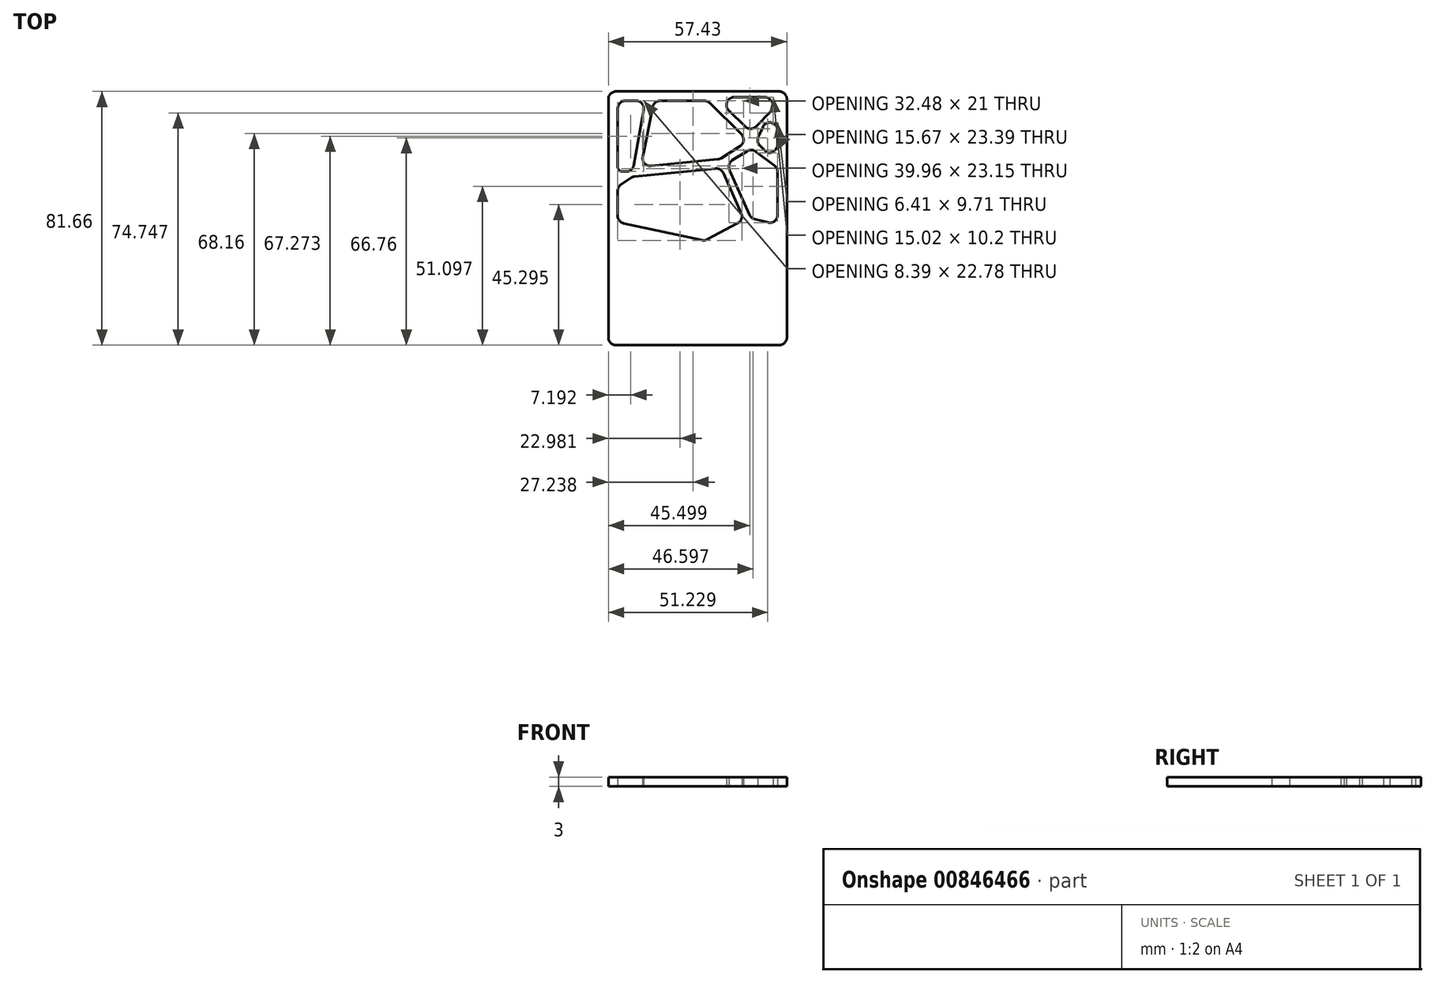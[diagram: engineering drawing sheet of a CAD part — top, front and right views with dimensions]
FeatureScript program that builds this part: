
annotation { "Feature Type Name" : "Feature", "Feature Type Description" : "" }
export const myFeature = defineFeature(function(context is Context, id is Id, definition is map)
    precondition{}
    {
        {
            assignVariable(context, id + "F0", {"name" : "depth", "anyValue" : 3 * mm});
        }
        {
            var Q0;
            Q0=qCreatedBy(makeId("Top.planeOp"),FACE);
            var sketch = newSketch(context, id + "F1", { "sketchPlane" : qUnion([Q0])});
            skLineSegment(sketch, "E0", {"start": v(11.17, 31.6) * mm, "end": v(14.38, 33.7) * mm});
            skLineSegment(sketch, "E1", {"start": v(15.5, 34.1) * mm, "end": v(41.49, 36.69) * mm});
            skLineSegment(sketch, "E2", {"start": v(44.02, 35.22) * mm, "end": v(49.79, 22.3) * mm});
            skLineSegment(sketch, "E3", {"start": v(48.68, 19.07) * mm, "end": v(38.89, 13.85) * mm});
            skLineSegment(sketch, "E4", {"start": v(37.19, 13.6) * mm, "end": v(12.02, 19) * mm});
            skPoint(sketch, "E5.visualSharp", {"position": v(21.18, 34.67) * mm});
            skArc(sketch, "E5.filletArc", {"start": v(15.5, 34.1) * mm, "mid": v(14.91, 33.97) * mm, "end": v(14.38, 33.7) * mm});
            skPoint(sketch, "E6.visualSharp", {"position": v(43.28, 36.87) * mm});
            skArc(sketch, "E6.filletArc", {"start": v(44.02, 35.22) * mm, "mid": v(43, 36.36) * mm, "end": v(41.49, 36.69) * mm});
            skPoint(sketch, "E7.visualSharp", {"position": v(50.74, 20.17) * mm});
            skArc(sketch, "E7.filletArc", {"start": v(48.68, 19.07) * mm, "mid": v(49.87, 20.46) * mm, "end": v(49.79, 22.3) * mm});
            skPoint(sketch, "E8.visualSharp", {"position": v(38.08, 13.41) * mm});
            skArc(sketch, "E8.filletArc", {"start": v(37.19, 13.6) * mm, "mid": v(38.06, 13.58) * mm, "end": v(38.89, 13.85) * mm});
            skLineSegment(sketch, "E9", {"start": v(20.79, 37.49) * mm, "end": v(42.17, 39.62) * mm});
            skLineSegment(sketch, "E10", {"start": v(43.27, 40) * mm, "end": v(49.37, 43.86) * mm});
            skLineSegment(sketch, "E11", {"start": v(49.78, 47.76) * mm, "end": v(39.55, 57.78) * mm});
            skLineSegment(sketch, "E12", {"start": v(37.8, 58.5) * mm, "end": v(23.76, 58.5) * mm});
            skLineSegment(sketch, "E13", {"start": v(21.3, 56.48) * mm, "end": v(18.09, 40.47) * mm});
            skPoint(sketch, "E14.visualSharp", {"position": v(21.7, 58.5) * mm});
            skArc(sketch, "E14.filletArc", {"start": v(23.76, 58.5) * mm, "mid": v(22.17, 57.93) * mm, "end": v(21.3, 56.48) * mm});
            skPoint(sketch, "E15.visualSharp", {"position": v(17.42, 37.15) * mm});
            skArc(sketch, "E15.filletArc", {"start": v(18.09, 40.47) * mm, "mid": v(18.69, 38.3) * mm, "end": v(20.79, 37.49) * mm});
            skPoint(sketch, "E16.visualSharp", {"position": v(42.76, 39.68) * mm});
            skArc(sketch, "E16.filletArc", {"start": v(42.17, 39.62) * mm, "mid": v(42.74, 39.74) * mm, "end": v(43.27, 40) * mm});
            skPoint(sketch, "E17.visualSharp", {"position": v(38.82, 58.5) * mm});
            skArc(sketch, "E17.filletArc", {"start": v(39.55, 57.78) * mm, "mid": v(38.75, 58.3) * mm, "end": v(37.8, 58.5) * mm});
            skPoint(sketch, "E18.visualSharp", {"position": v(52.03, 45.55) * mm});
            skArc(sketch, "E18.filletArc", {"start": v(49.37, 43.86) * mm, "mid": v(50.52, 45.71) * mm, "end": v(49.78, 47.76) * mm});
            skPoint(sketch, "E19", {"position": v(30.78, 58.5) * mm});
            skLineSegment(sketch, "E20", {"start": v(47, 39.4) * mm, "end": v(51.65, 42.26) * mm});
            skLineSegment(sketch, "E21", {"start": v(46.01, 36.26) * mm, "end": v(52.48, 21.76) * mm});
            skLineSegment(sketch, "E22", {"start": v(54.16, 20.35) * mm, "end": v(58.37, 19.3) * mm});
            skLineSegment(sketch, "E23", {"start": v(61.47, 21.73) * mm, "end": v(61.47, 33.28) * mm});
            skLineSegment(sketch, "E24", {"start": v(61.47, 33.32) * mm, "end": v(61.44, 35.64) * mm});
            skLineSegment(sketch, "E25", {"start": v(60.45, 37.6) * mm, "end": v(54.46, 42.12) * mm});
            skPoint(sketch, "E26.visualSharp", {"position": v(53.1, 43.15) * mm});
            skArc(sketch, "E26.filletArc", {"start": v(54.46, 42.12) * mm, "mid": v(53.08, 42.62) * mm, "end": v(51.65, 42.26) * mm});
            skPoint(sketch, "E27.visualSharp", {"position": v(45.12, 38.26) * mm});
            skArc(sketch, "E27.filletArc", {"start": v(47, 39.4) * mm, "mid": v(45.9, 38.02) * mm, "end": v(46.01, 36.26) * mm});
            skPoint(sketch, "E28.visualSharp", {"position": v(52.98, 20.65) * mm});
            skArc(sketch, "E28.filletArc", {"start": v(52.48, 21.76) * mm, "mid": v(53.16, 20.86) * mm, "end": v(54.16, 20.35) * mm});
            skPoint(sketch, "E29.visualSharp", {"position": v(61.47, 18.53) * mm});
            skArc(sketch, "E29.filletArc", {"start": v(58.37, 19.3) * mm, "mid": v(60.51, 19.76) * mm, "end": v(61.47, 21.73) * mm});
            skPoint(sketch, "E30.visualSharp", {"position": v(61.47, 33.3) * mm});
            skArc(sketch, "E30.filletArc", {"start": v(61.47, 33.28) * mm, "mid": v(61.47, 33.3) * mm, "end": v(61.47, 33.32) * mm});
            skPoint(sketch, "E31.visualSharp", {"position": v(61.42, 36.87) * mm});
            skArc(sketch, "E31.filletArc", {"start": v(61.44, 35.64) * mm, "mid": v(61.17, 36.74) * mm, "end": v(60.45, 37.6) * mm});
            skLineSegment(sketch, "E32", {"start": v(10.04, 21.45) * mm, "end": v(10.04, 29.51) * mm});
            skPoint(sketch, "E33.visualSharp", {"position": v(10.04, 30.86) * mm});
            skArc(sketch, "E33.filletArc", {"start": v(11.17, 31.6) * mm, "mid": v(10.34, 30.7) * mm, "end": v(10.04, 29.51) * mm});
            skLineSegment(sketch, "E34", {"start": v(7.04, 59) * mm, "end": v(7.04, -17.67) * mm});
            skLineSegment(sketch, "E35", {"start": v(64.47, -17.67) * mm, "end": v(64.47, 59) * mm});
            skPoint(sketch, "E36.visualSharp", {"position": v(10.04, 19.43) * mm});
            skArc(sketch, "E36.filletArc", {"start": v(10.04, 21.45) * mm, "mid": v(10.6, 19.88) * mm, "end": v(12.02, 19) * mm});
            skLineSegment(sketch, "E37", {"start": v(9.54, -20.17) * mm, "end": v(61.97, -20.17) * mm});
            skPoint(sketch, "E38.visualSharp", {"position": v(7.04, -20.17) * mm});
            skArc(sketch, "E38.filletArc", {"start": v(7.04, -17.67) * mm, "mid": v(7.77, -19.44) * mm, "end": v(9.54, -20.17) * mm});
            skPoint(sketch, "E39.visualSharp", {"position": v(64.47, -20.17) * mm});
            skArc(sketch, "E39.filletArc", {"start": v(61.97, -20.17) * mm, "mid": v(63.74, -19.44) * mm, "end": v(64.47, -17.67) * mm});
            skLineSegment(sketch, "E40", {"start": v(9.54, 61.5) * mm, "end": v(61.97, 61.5) * mm});
            skPoint(sketch, "E41.visualSharp", {"position": v(7.04, 61.5) * mm});
            skArc(sketch, "E41.filletArc", {"start": v(9.54, 61.5) * mm, "mid": v(7.77, 60.76) * mm, "end": v(7.04, 59) * mm});
            skPoint(sketch, "E42.visualSharp", {"position": v(64.47, 61.5) * mm});
            skArc(sketch, "E42.filletArc", {"start": v(64.47, 59) * mm, "mid": v(63.74, 60.76) * mm, "end": v(61.97, 61.5) * mm});
            skLineSegment(sketch, "E43", {"start": v(45.77, 55.34) * mm, "end": v(51.03, 50.2) * mm});
            skLineSegment(sketch, "E44", {"start": v(54.56, 50.23) * mm, "end": v(59.34, 55.1) * mm});
            skLineSegment(sketch, "E45", {"start": v(59.3, 58.64) * mm, "end": v(58.97, 58.96) * mm});
            skLineSegment(sketch, "E46", {"start": v(57.2, 59.68) * mm, "end": v(47.5, 59.63) * mm});
            skLineSegment(sketch, "E47", {"start": v(55.81, 43.98) * mm, "end": v(57.52, 42.3) * mm});
            skLineSegment(sketch, "E48", {"start": v(60.35, 42.34) * mm, "end": v(60.76, 42.75) * mm});
            skLineSegment(sketch, "E49", {"start": v(61.47, 44.5) * mm, "end": v(61.47, 48.97) * mm});
            skLineSegment(sketch, "E50", {"start": v(56.69, 49.98) * mm, "end": v(55.27, 46.78) * mm});
            skLineSegment(sketch, "E51", {"start": v(18.39, 55.56) * mm, "end": v(15.25, 37.78) * mm});
            skLineSegment(sketch, "E52", {"start": v(12.79, 35.71) * mm, "end": v(11.54, 35.71) * mm});
            skLineSegment(sketch, "E53", {"start": v(10.04, 37.21) * mm, "end": v(10.04, 56) * mm});
            skLineSegment(sketch, "E54", {"start": v(12.54, 58.5) * mm, "end": v(15.93, 58.5) * mm});
            skPoint(sketch, "E55.visualSharp", {"position": v(10.04, 58.5) * mm});
            skArc(sketch, "E55.filletArc", {"start": v(12.54, 58.5) * mm, "mid": v(10.77, 57.76) * mm, "end": v(10.04, 56) * mm});
            skPoint(sketch, "E56.visualSharp", {"position": v(18.9, 58.5) * mm});
            skArc(sketch, "E56.filletArc", {"start": v(18.39, 55.56) * mm, "mid": v(17.84, 57.6) * mm, "end": v(15.93, 58.5) * mm});
            skPoint(sketch, "E57.visualSharp", {"position": v(14.88, 35.71) * mm});
            skArc(sketch, "E57.filletArc", {"start": v(12.79, 35.71) * mm, "mid": v(14.4, 36.3) * mm, "end": v(15.25, 37.78) * mm});
            skPoint(sketch, "E58.visualSharp", {"position": v(10.04, 35.71) * mm});
            skArc(sketch, "E58.filletArc", {"start": v(10.04, 37.21) * mm, "mid": v(10.48, 36.15) * mm, "end": v(11.54, 35.71) * mm});
            skPoint(sketch, "E59.visualSharp", {"position": v(41.42, 59.6) * mm});
            skArc(sketch, "E59.filletArc", {"start": v(47.5, 59.63) * mm, "mid": v(45.2, 58.07) * mm, "end": v(45.77, 55.34) * mm});
            skPoint(sketch, "E60.visualSharp", {"position": v(52.81, 48.44) * mm});
            skArc(sketch, "E60.filletArc", {"start": v(51.03, 50.2) * mm, "mid": v(52.8, 49.48) * mm, "end": v(54.56, 50.23) * mm});
            skPoint(sketch, "E61.visualSharp", {"position": v(61.09, 56.89) * mm});
            skArc(sketch, "E61.filletArc", {"start": v(59.34, 55.1) * mm, "mid": v(60.05, 56.88) * mm, "end": v(59.3, 58.64) * mm});
            skPoint(sketch, "E62.visualSharp", {"position": v(58.23, 59.68) * mm});
            skArc(sketch, "E62.filletArc", {"start": v(58.97, 58.96) * mm, "mid": v(58.16, 59.5) * mm, "end": v(57.2, 59.68) * mm});
            skPoint(sketch, "E63.visualSharp", {"position": v(61.47, 60.82) * mm});
            skArc(sketch, "E63.filletArc", {"start": v(61.47, 48.97) * mm, "mid": v(59.49, 51.41) * mm, "end": v(56.69, 49.98) * mm});
            skPoint(sketch, "E64.visualSharp", {"position": v(54.58, 45.2) * mm});
            skArc(sketch, "E64.filletArc", {"start": v(55.27, 46.78) * mm, "mid": v(55.1, 45.3) * mm, "end": v(55.81, 43.98) * mm});
            skPoint(sketch, "E65.visualSharp", {"position": v(61.47, 43.48) * mm});
            skArc(sketch, "E65.filletArc", {"start": v(60.76, 42.75) * mm, "mid": v(61.29, 43.56) * mm, "end": v(61.47, 44.5) * mm});
            skPoint(sketch, "E66.visualSharp", {"position": v(58.95, 40.9) * mm});
            skArc(sketch, "E66.filletArc", {"start": v(57.52, 42.3) * mm, "mid": v(58.94, 41.74) * mm, "end": v(60.35, 42.34) * mm});
            skSolve(sketch);
        }
        {
            var Q0;
            Q0 = qSketchRegion(id + "F1", true);
            extrude(context, id + "F2", {"entities" : qUnion([Q0]), "depth" : getVariable(context, 'depth'), "offsetDistance" : 25 * mm});
        }
        {
            var Q0;
            Q0=makeQuery(id+"F2.opExtrude","SWEPT_BODY",BODY,{"disambiguationData":[OSD([sQuery(id+"F1.wireOp",EDGE,"E0"),sQuery(id+"F1.wireOp",EDGE,"E1"),sQuery(id+"F1.wireOp",EDGE,"E2"),sQuery(id+"F1.wireOp",EDGE,"E3"),sQuery(id+"F1.wireOp",EDGE,"E4"),sQuery(id+"F1.wireOp",EDGE,"E5.filletArc"),sQuery(id+"F1.wireOp",EDGE,"E6.filletArc"),sQuery(id+"F1.wireOp",EDGE,"E7.filletArc"),sQuery(id+"F1.wireOp",EDGE,"E8.filletArc"),sQuery(id+"F1.wireOp",EDGE,"E9"),sQuery(id+"F1.wireOp",EDGE,"E10"),sQuery(id+"F1.wireOp",EDGE,"E11"),sQuery(id+"F1.wireOp",EDGE,"E12"),sQuery(id+"F1.wireOp",EDGE,"E13"),sQuery(id+"F1.wireOp",EDGE,"E14.filletArc"),sQuery(id+"F1.wireOp",EDGE,"E15.filletArc"),sQuery(id+"F1.wireOp",EDGE,"E16.filletArc"),sQuery(id+"F1.wireOp",EDGE,"E17.filletArc"),sQuery(id+"F1.wireOp",EDGE,"E18.filletArc"),sQuery(id+"F1.wireOp",EDGE,"E20"),sQuery(id+"F1.wireOp",EDGE,"E21"),sQuery(id+"F1.wireOp",EDGE,"E22"),sQuery(id+"F1.wireOp",EDGE,"E23"),sQuery(id+"F1.wireOp",EDGE,"E24"),sQuery(id+"F1.wireOp",EDGE,"E25"),sQuery(id+"F1.wireOp",EDGE,"E26.filletArc"),sQuery(id+"F1.wireOp",EDGE,"E27.filletArc"),sQuery(id+"F1.wireOp",EDGE,"E28.filletArc"),sQuery(id+"F1.wireOp",EDGE,"E29.filletArc"),sQuery(id+"F1.wireOp",EDGE,"E30.filletArc"),sQuery(id+"F1.wireOp",EDGE,"E31.filletArc"),sQuery(id+"F1.wireOp",EDGE,"E32"),sQuery(id+"F1.wireOp",EDGE,"E33.filletArc"),sQuery(id+"F1.wireOp",EDGE,"E34"),sQuery(id+"F1.wireOp",EDGE,"E35"),sQuery(id+"F1.wireOp",EDGE,"E36.filletArc"),sQuery(id+"F1.wireOp",EDGE,"E37"),sQuery(id+"F1.wireOp",EDGE,"E38.filletArc"),sQuery(id+"F1.wireOp",EDGE,"E39.filletArc"),sQuery(id+"F1.wireOp",EDGE,"E40"),sQuery(id+"F1.wireOp",EDGE,"E41.filletArc"),sQuery(id+"F1.wireOp",EDGE,"E42.filletArc"),sQuery(id+"F1.wireOp",EDGE,"E43"),sQuery(id+"F1.wireOp",EDGE,"E44"),sQuery(id+"F1.wireOp",EDGE,"E45"),sQuery(id+"F1.wireOp",EDGE,"E46"),sQuery(id+"F1.wireOp",EDGE,"E47"),sQuery(id+"F1.wireOp",EDGE,"E48"),sQuery(id+"F1.wireOp",EDGE,"E49"),sQuery(id+"F1.wireOp",EDGE,"E50"),sQuery(id+"F1.wireOp",EDGE,"E51"),sQuery(id+"F1.wireOp",EDGE,"E52"),sQuery(id+"F1.wireOp",EDGE,"E53"),sQuery(id+"F1.wireOp",EDGE,"E54"),sQuery(id+"F1.wireOp",EDGE,"E55.filletArc"),sQuery(id+"F1.wireOp",EDGE,"E56.filletArc"),sQuery(id+"F1.wireOp",EDGE,"E57.filletArc"),sQuery(id+"F1.wireOp",EDGE,"E58.filletArc"),sQuery(id+"F1.wireOp",EDGE,"E59.filletArc"),sQuery(id+"F1.wireOp",EDGE,"E60.filletArc"),sQuery(id+"F1.wireOp",EDGE,"E61.filletArc"),sQuery(id+"F1.wireOp",EDGE,"E62.filletArc"),sQuery(id+"F1.wireOp",EDGE,"E63.filletArc"),sQuery(id+"F1.wireOp",EDGE,"E64.filletArc"),sQuery(id+"F1.wireOp",EDGE,"E65.filletArc"),sQuery(id+"F1.wireOp",EDGE,"E66.filletArc")])]});
            var Q1;
            Q1=makeQuery(id+"F2.opExtrude","CAP_EDGE",EDGE,{"disambiguationData":[OSD([sQuery(id+"F1.wireOp",EDGE,"E37")])],"isStart":false});
            transform(context, id + "F3", {"entities" : qUnion([Q0]), "transformType" : TransformType.ROTATION, "transformAxis" : qUnion([Q1]), "angle" : 180 * degree, "oppositeDirection" : true, "makeCopy" : true});
        }
        {
            var Q0;
            Q0=makeQuery(id+"F3.opPattern","COPY",BODY,{"derivedFrom":makeQuery(id+"F2.opExtrude","SWEPT_BODY",BODY,{"disambiguationData":[OSD([sQuery(id+"F1.wireOp",EDGE,"E0"),sQuery(id+"F1.wireOp",EDGE,"E1"),sQuery(id+"F1.wireOp",EDGE,"E2"),sQuery(id+"F1.wireOp",EDGE,"E3"),sQuery(id+"F1.wireOp",EDGE,"E4"),sQuery(id+"F1.wireOp",EDGE,"E5.filletArc"),sQuery(id+"F1.wireOp",EDGE,"E6.filletArc"),sQuery(id+"F1.wireOp",EDGE,"E7.filletArc"),sQuery(id+"F1.wireOp",EDGE,"E8.filletArc"),sQuery(id+"F1.wireOp",EDGE,"E9"),sQuery(id+"F1.wireOp",EDGE,"E10"),sQuery(id+"F1.wireOp",EDGE,"E11"),sQuery(id+"F1.wireOp",EDGE,"E12"),sQuery(id+"F1.wireOp",EDGE,"E13"),sQuery(id+"F1.wireOp",EDGE,"E14.filletArc"),sQuery(id+"F1.wireOp",EDGE,"E15.filletArc"),sQuery(id+"F1.wireOp",EDGE,"E16.filletArc"),sQuery(id+"F1.wireOp",EDGE,"E17.filletArc"),sQuery(id+"F1.wireOp",EDGE,"E18.filletArc"),sQuery(id+"F1.wireOp",EDGE,"E20"),sQuery(id+"F1.wireOp",EDGE,"E21"),sQuery(id+"F1.wireOp",EDGE,"E22"),sQuery(id+"F1.wireOp",EDGE,"E23"),sQuery(id+"F1.wireOp",EDGE,"E24"),sQuery(id+"F1.wireOp",EDGE,"E25"),sQuery(id+"F1.wireOp",EDGE,"E26.filletArc"),sQuery(id+"F1.wireOp",EDGE,"E27.filletArc"),sQuery(id+"F1.wireOp",EDGE,"E28.filletArc"),sQuery(id+"F1.wireOp",EDGE,"E29.filletArc"),sQuery(id+"F1.wireOp",EDGE,"E30.filletArc"),sQuery(id+"F1.wireOp",EDGE,"E31.filletArc"),sQuery(id+"F1.wireOp",EDGE,"E32"),sQuery(id+"F1.wireOp",EDGE,"E33.filletArc"),sQuery(id+"F1.wireOp",EDGE,"E34"),sQuery(id+"F1.wireOp",EDGE,"E35"),sQuery(id+"F1.wireOp",EDGE,"E36.filletArc"),sQuery(id+"F1.wireOp",EDGE,"E37"),sQuery(id+"F1.wireOp",EDGE,"E38.filletArc"),sQuery(id+"F1.wireOp",EDGE,"E39.filletArc"),sQuery(id+"F1.wireOp",EDGE,"E40"),sQuery(id+"F1.wireOp",EDGE,"E41.filletArc"),sQuery(id+"F1.wireOp",EDGE,"E42.filletArc"),sQuery(id+"F1.wireOp",EDGE,"E43"),sQuery(id+"F1.wireOp",EDGE,"E44"),sQuery(id+"F1.wireOp",EDGE,"E45"),sQuery(id+"F1.wireOp",EDGE,"E46"),sQuery(id+"F1.wireOp",EDGE,"E47"),sQuery(id+"F1.wireOp",EDGE,"E48"),sQuery(id+"F1.wireOp",EDGE,"E49"),sQuery(id+"F1.wireOp",EDGE,"E50"),sQuery(id+"F1.wireOp",EDGE,"E51"),sQuery(id+"F1.wireOp",EDGE,"E52"),sQuery(id+"F1.wireOp",EDGE,"E53"),sQuery(id+"F1.wireOp",EDGE,"E54"),sQuery(id+"F1.wireOp",EDGE,"E55.filletArc"),sQuery(id+"F1.wireOp",EDGE,"E56.filletArc"),sQuery(id+"F1.wireOp",EDGE,"E57.filletArc"),sQuery(id+"F1.wireOp",EDGE,"E58.filletArc"),sQuery(id+"F1.wireOp",EDGE,"E59.filletArc"),sQuery(id+"F1.wireOp",EDGE,"E60.filletArc"),sQuery(id+"F1.wireOp",EDGE,"E61.filletArc"),sQuery(id+"F1.wireOp",EDGE,"E62.filletArc"),sQuery(id+"F1.wireOp",EDGE,"E63.filletArc"),sQuery(id+"F1.wireOp",EDGE,"E64.filletArc"),sQuery(id+"F1.wireOp",EDGE,"E65.filletArc"),sQuery(id+"F1.wireOp",EDGE,"E66.filletArc")])]}),"instanceName":"1"});
            deleteBodies(context, id + "F4", {"entities" : qUnion([Q0])});
        }
    });
